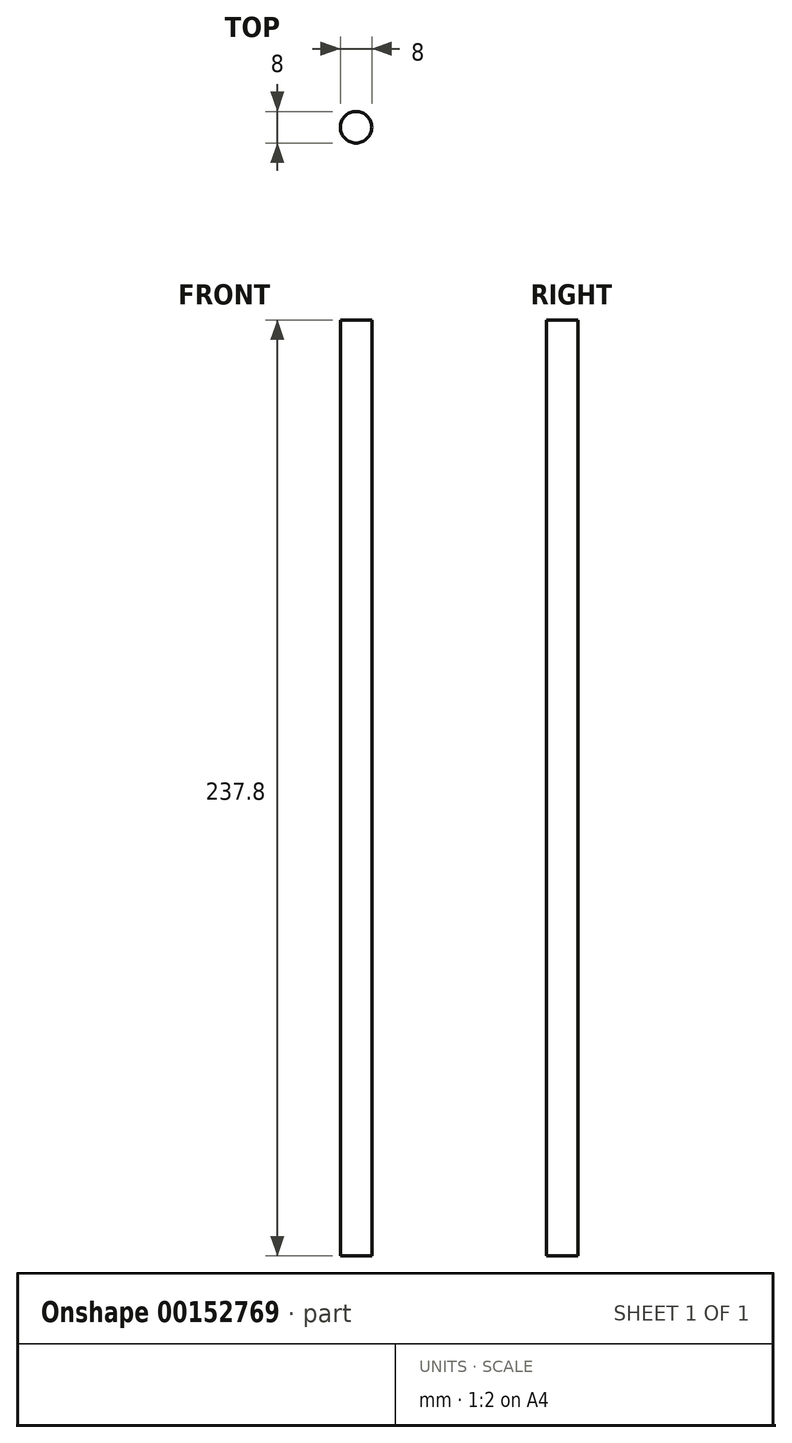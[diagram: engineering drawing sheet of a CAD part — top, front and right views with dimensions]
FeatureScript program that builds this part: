
annotation { "Feature Type Name" : "Feature", "Feature Type Description" : "" }
export const myFeature = defineFeature(function(context is Context, id is Id, definition is map)
    precondition{}
    {
        {
            var Q0;
            Q0=qCreatedBy(makeId("Top.planeOp"),FACE);
            var sketch = newSketch(context, id + "F0", { "sketchPlane" : qUnion([Q0])});
            skCircle(sketch, "E0", {"center": v(0, 0) * mm, "radius": 4 * mm});
            skSolve(sketch);
        }
        {
            var Q0;
            Q0 = qSketchRegion(id + "F0", true);
            extrude(context, id + "F1", {"entities" : qUnion([Q0]), "depth" : 237.8 * mm});
        }
    });
